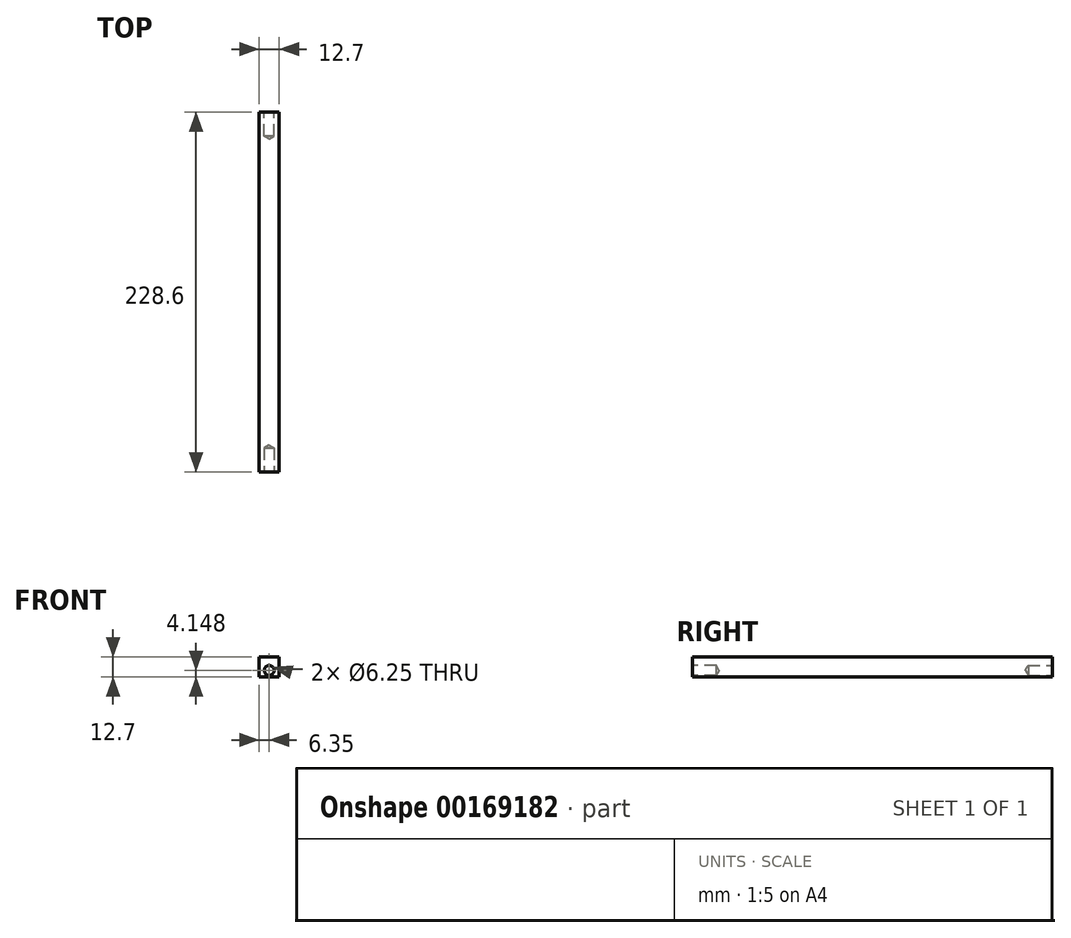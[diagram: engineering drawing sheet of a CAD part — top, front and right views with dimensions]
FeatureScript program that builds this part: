
annotation { "Feature Type Name" : "Feature", "Feature Type Description" : "" }
export const myFeature = defineFeature(function(context is Context, id is Id, definition is map)
    precondition{}
    {
        {
            var Q0;
            Q0=qCreatedBy(makeId("Front.planeOp"),FACE);
            var sketch = newSketch(context, id + "F0", { "sketchPlane" : qUnion([Q0])});
            skLineSegment(sketch, "E0.bottom", {"start": v(0, 0) * mm, "end": v(12.7, 0) * mm});
            skLineSegment(sketch, "E0.top", {"start": v(0, 12.7) * mm, "end": v(12.7, 12.7) * mm});
            skLineSegment(sketch, "E0.left", {"start": v(0, 0) * mm, "end": v(0, 12.7) * mm});
            skLineSegment(sketch, "E0.right", {"start": v(12.7, 0) * mm, "end": v(12.7, 12.7) * mm});
            skSolve(sketch);
        }
        {
            var Q0;
            Q0=makeQuery(id+"F0.imprint","IMPRINT",FACE,{"disambiguationData":[TD([[makeQuery(id+"F0.imprint","IMPRINT",EDGE,{"derivedFrom":sQuery(id+"F0.wireOp",EDGE,"E0.bottom")}),1.0]])]});
            extrude(context, id + "F1", {"entities" : qUnion([Q0]), "depth" : 228.6 * mm});
        }
        {
            var Q0;
            Q0=makeQuery(id+"F1.opExtrude","CAP_FACE",FACE,{"disambiguationData":[OSD([sQuery(id+"F0.wireOp",EDGE,"E0.bottom"),sQuery(id+"F0.wireOp",EDGE,"E0.top"),sQuery(id+"F0.wireOp",EDGE,"E0.left"),sQuery(id+"F0.wireOp",EDGE,"E0.right")])],"isStart":false});
            var sketch = newSketch(context, id + "F2", { "sketchPlane" : qUnion([Q0])});
            skPoint(sketch, "E1", {"position": v(6.35, 4.15) * mm});
            skPoint(sketch, "E1.positionSnap0", {"position": v(6.35, 12.7) * mm});
            skPoint(sketch, "E1.positionSnap1", {"position": v(0, 6.35) * mm});
            skSolve(sketch);
        }
        {
            var Q0;
            Q0=sQuery(id+"F2.wireOp",VERTEX,"E1");
            var Q1;
            Q1=makeQuery(id+"F1.opExtrude","SWEPT_BODY",BODY,{"disambiguationData":[OSD([sQuery(id+"F0.wireOp",EDGE,"E0.bottom"),sQuery(id+"F0.wireOp",EDGE,"E0.top"),sQuery(id+"F0.wireOp",EDGE,"E0.left"),sQuery(id+"F0.wireOp",EDGE,"E0.right")])]});
            hole(context, id + "F3", {"style" : HoleStyle.SIMPLE, "endStyle" : HoleEndStyle.BLIND, "standardTappedOrClearance" : lookupTablePath({ "standard" : "ANSI", "size" : "D (0.25)", "type" : "Drilled" }), "standardBlindInLast" : lookupTablePath({ "standard" : "ANSI", "size" : "D", "type" : "Drilled" }), "holeDiameter" : 6.25 * mm, "holeDepth" : 15.24 * mm, "startFromSketch" : true, "locations" : qUnion([Q0]), "scope" : qUnion([Q1])});
        }
        {
            var Q0;
            Q0=makeQuery(id+"F1.opExtrude","CAP_FACE",FACE,{"disambiguationData":[OSD([sQuery(id+"F0.wireOp",EDGE,"E0.bottom"),sQuery(id+"F0.wireOp",EDGE,"E0.top"),sQuery(id+"F0.wireOp",EDGE,"E0.left"),sQuery(id+"F0.wireOp",EDGE,"E0.right")])],"isStart":true});
            var sketch = newSketch(context, id + "F4", { "sketchPlane" : qUnion([Q0])});
            skPoint(sketch, "E2", {"position": v(-6.35, 4.15) * mm});
            skPoint(sketch, "E2.positionSnap0", {"position": v(0, 6.35) * mm});
            skPoint(sketch, "E2.positionSnap1", {"position": v(-6.35, 12.7) * mm});
            skSolve(sketch);
        }
        {
            var Q0;
            Q0=sQuery(id+"F4.wireOp",VERTEX,"E2");
            var Q1;
            Q1=makeQuery(id+"F1.opExtrude","SWEPT_BODY",BODY,{"disambiguationData":[OSD([sQuery(id+"F0.wireOp",EDGE,"E0.bottom"),sQuery(id+"F0.wireOp",EDGE,"E0.top"),sQuery(id+"F0.wireOp",EDGE,"E0.left"),sQuery(id+"F0.wireOp",EDGE,"E0.right")])]});
            hole(context, id + "F5", {"style" : HoleStyle.SIMPLE, "endStyle" : HoleEndStyle.BLIND, "standardTappedOrClearance" : lookupTablePath({ "standard" : "ANSI", "size" : "D (0.25)", "type" : "Drilled" }), "standardBlindInLast" : lookupTablePath({ "standard" : "ANSI", "size" : "D", "type" : "Drilled" }), "holeDiameter" : 6.25 * mm, "holeDepth" : 15.24 * mm, "startFromSketch" : true, "locations" : qUnion([Q0]), "scope" : qUnion([Q1])});
        }
    });
